# Revit family: Schmutzfänger 4111
name_source: partatom
category: Rohrzubehör
revit_build: Autodesk Revit 2018 (Build: 20190510_1515(x64)
units: mm (PartAtom-declared; Revit-internal decimal feet)

## family parameters
Arbeitsebenenbasiert = Nein
Beim Laden mit Abzugskörper schneiden = Nein
Bemaßung runder Anschluss = Durchmesser verwenden
Gemeinsam genutzt = Nein
Immer vertikal = Ja
OmniClass-Nummer = 23.65.55.14
OmniClass-Titel = Valves for Liquid Services
Teiletyp = Unterbricht

## types (1)
- Schmutzfänger 4111
    Anwendungen = Für Flüssigkeiten in Warm- und Kaltwassersystemen
    Aufsatz = GG25
    Dichtung = Klingerit
    Filter (DN100-DN400) = AISI 304, Maschenweite 1500 μm
    Filter (DN50-DN80) = AISI 304, Maschenweite 600 μm
    Gehäuse = GG25
    Hersteller = HERZ Armaturen Ges.m.b.H.
    Max.Betriebstemperatur = 120 °C
    Medium = Heizwasserqualität nach ÖNORM H5195 oder VDI-Standard 2035.
Die Verwendung von Ethylen oder Propylenglykol im Mischungsverhältnis von 25-50% ist zulässig.
    Min.Betriebstemperatur = -10 °C
    PN = 1600000.0 Pa
    SCRNCODE = 05;15;02
    SCRNSEQ = AWI;AWI_TYP="1011";2
    URL = www.herz-armaturen.at
    Verschluss = St37
    Verschlussdichtung = Kupfer
    W01 = 140.00°
    W02 = 45.00°
    Zwischenrahmen = Edelstahl
